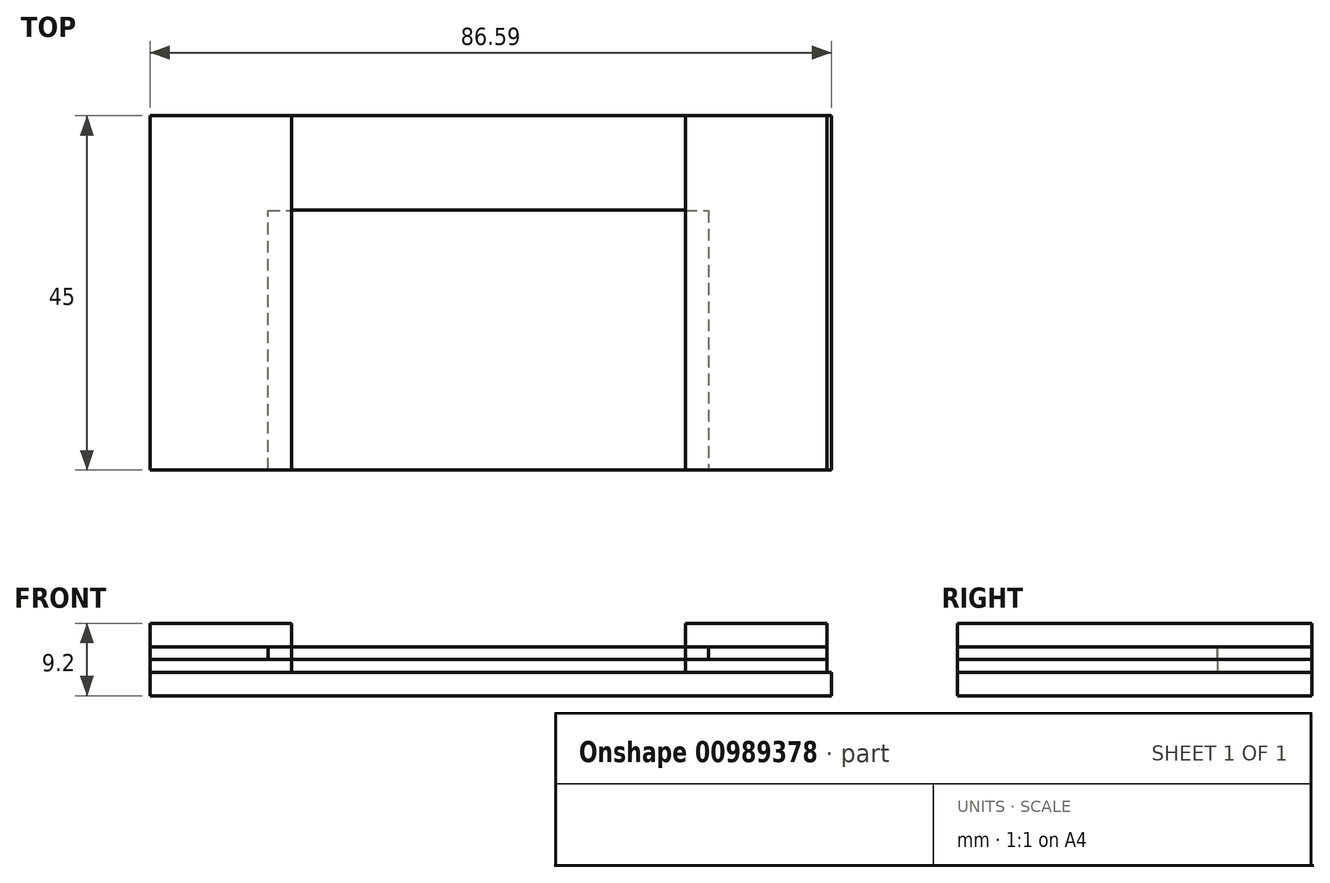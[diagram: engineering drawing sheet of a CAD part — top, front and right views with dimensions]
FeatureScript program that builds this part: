
annotation { "Feature Type Name" : "Feature", "Feature Type Description" : "" }
export const myFeature = defineFeature(function(context is Context, id is Id, definition is map)
    precondition{}
    {
        {
            var Q0;
            Q0=qCreatedBy(makeId("Top.planeOp"),FACE);
            var sketch = newSketch(context, id + "F0", { "sketchPlane" : qUnion([Q0])});
            skLineSegment(sketch, "E0.bottom", {"start": v(43, 22.5) * mm, "end": v(-43, 22.5) * mm});
            skLineSegment(sketch, "E0.top", {"start": v(43, -22.5) * mm, "end": v(25, -22.5) * mm});
            skLineSegment(sketch, "E0.left", {"start": v(43, 22.5) * mm, "end": v(43, -22.5) * mm});
            skLineSegment(sketch, "E0.right", {"start": v(-43, 22.5) * mm, "end": v(-43, -22.5) * mm});
            skPoint(sketch, "E0.middle", {"position": v(0, 0) * mm});
            skLineSegment(sketch, "E1", {"start": v(-25, -22.5) * mm, "end": v(-25, 10.5) * mm});
            skLineSegment(sketch, "E2", {"start": v(-25, 10.5) * mm, "end": v(25, 10.5) * mm});
            skLineSegment(sketch, "E3", {"start": v(25, 10.5) * mm, "end": v(25, -22.5) * mm});
            skLineSegment(sketch, "E4", {"start": v(25, -22.5) * mm, "end": v(24.29, -21.86) * mm});
            skLineSegment(sketch, "E5.trimOffspring", {"start": v(-25, -22.5) * mm, "end": v(-43, -22.5) * mm});
            skSolve(sketch);
        }
        {
            var Q0;
            Q0 = qSketchRegion(id + "F0", true);
            extrude(context, id + "F1", {"entities" : qUnion([Q0]), "depth" : 1.6 * mm, "offsetDistance" : 25 * mm});
        }
        {
            var Q0;
            Q0=makeQuery(id+"F1.opExtrude","CAP_FACE",FACE,{"disambiguationData":[OSD([sQuery(id+"F0.wireOp",EDGE,"E0.bottom"),sQuery(id+"F0.wireOp",EDGE,"E0.top"),sQuery(id+"F0.wireOp",EDGE,"E0.left"),sQuery(id+"F0.wireOp",EDGE,"E0.right")])],"isStart":false});
            var sketch = newSketch(context, id + "F2", { "sketchPlane" : qUnion([Q0])});
            skLineSegment(sketch, "E6.bottom", {"start": v(43, 22.5) * mm, "end": v(-43, 22.5) * mm});
            skLineSegment(sketch, "E6.top", {"start": v(43, -22.5) * mm, "end": v(43, -22.5) * mm});
            skLineSegment(sketch, "E6.left", {"start": v(43, 22.5) * mm, "end": v(43, -22.5) * mm});
            skLineSegment(sketch, "E6.right", {"start": v(-43, 22.5) * mm, "end": v(-43, -22.5) * mm});
            skPoint(sketch, "E6.middle", {"position": v(0, 0) * mm});
            skLineSegment(sketch, "E7.top", {"start": v(43, -22.5) * mm, "end": v(-43, -22.5) * mm});
            skLineSegment(sketch, "E8.trimOffspring", {"start": v(-43, -22.5) * mm, "end": v(-43, -22.5) * mm});
            skLineSegment(sketch, "E9", {"start": v(-27.97, -22.5) * mm, "end": v(-27.97, 10.42) * mm});
            skLineSegment(sketch, "E10", {"start": v(-27.97, 10.42) * mm, "end": v(27.97, 10.42) * mm});
            skLineSegment(sketch, "E11", {"start": v(27.97, 10.42) * mm, "end": v(27.97, -22.5) * mm});
            skSolve(sketch);
        }
        {
            var Q0;
            Q0=makeQuery(id+"F2.imprint","IMPRINT",FACE,{"disambiguationData":[TD([[makeQuery(id+"F2.imprint","IMPRINT",EDGE,{"derivedFrom":sQuery(id+"F2.wireOp",EDGE,"E6.bottom")}),1.0]])]});
            extrude(context, id + "F3", {"entities" : qUnion([Q0]), "depth" : 1.6 * mm, "offsetDistance" : 25 * mm});
        }
        {
            var Q0;
            Q0=makeQuery(id+"F3.opExtrude","CAP_FACE",FACE,{"disambiguationData":[OSD([sQuery(id+"F2.wireOp",EDGE,"E6.bottom"),sQuery(id+"F2.wireOp",EDGE,"E6.top"),sQuery(id+"F2.wireOp",EDGE,"E6.left"),sQuery(id+"F2.wireOp",EDGE,"E6.right"),sQuery(id+"F2.wireOp",EDGE,"E6.bottom"),sQuery(id+"F2.wireOp",EDGE,"E6.left"),sQuery(id+"F2.wireOp",EDGE,"E6.right"),sQuery(id+"F2.wireOp",EDGE,"E8.trimOffspring")])],"isStart":false});
            var sketch = newSketch(context, id + "F4", { "sketchPlane" : qUnion([Q0])});
            skLineSegment(sketch, "E12.bottom", {"start": v(-43, 22.5) * mm, "end": v(-25, 22.5) * mm});
            skLineSegment(sketch, "E12.top", {"start": v(-43, -22.5) * mm, "end": v(-25, -22.5) * mm});
            skLineSegment(sketch, "E12.left", {"start": v(-43, 22.5) * mm, "end": v(-43, -22.5) * mm});
            skLineSegment(sketch, "E12.right", {"start": v(-25, 22.5) * mm, "end": v(-25, -22.5) * mm});
            skLineSegment(sketch, "E13.bottom", {"start": v(43, 22.5) * mm, "end": v(25, 22.5) * mm});
            skLineSegment(sketch, "E13.top", {"start": v(43, -22.5) * mm, "end": v(25, -22.5) * mm});
            skLineSegment(sketch, "E13.left", {"start": v(43, 22.5) * mm, "end": v(43, -22.5) * mm});
            skLineSegment(sketch, "E13.right", {"start": v(25, 22.5) * mm, "end": v(25, -22.5) * mm});
            skSolve(sketch);
        }
        {
            var Q0;
            Q0 = qSketchRegion(id + "F4", true);
            extrude(context, id + "F5", {"entities" : qUnion([Q0]), "depth" : 3 * mm, "offsetDistance" : 25 * mm});
        }
        {
            var Q0;
            Q0=qCreatedBy(makeId("Top.planeOp"),FACE);
            var sketch = newSketch(context, id + "F6", { "sketchPlane" : qUnion([Q0])});
            skLineSegment(sketch, "E14.bottom", {"start": v(-43, -22.5) * mm, "end": v(43.59, -22.5) * mm});
            skLineSegment(sketch, "E14.top", {"start": v(-43, 22.5) * mm, "end": v(43.59, 22.5) * mm});
            skLineSegment(sketch, "E14.left", {"start": v(-43, -22.5) * mm, "end": v(-43, 22.5) * mm});
            skLineSegment(sketch, "E14.right", {"start": v(43.59, -22.5) * mm, "end": v(43.59, 22.5) * mm});
            skSolve(sketch);
        }
        {
            var Q0;
            Q0 = qSketchRegion(id + "F6", true);
            extrude(context, id + "F7", {"entities" : qUnion([Q0]), "oppositeDirection" : true, "depth" : 3 * mm, "offsetDistance" : 25 * mm});
        }
    });
